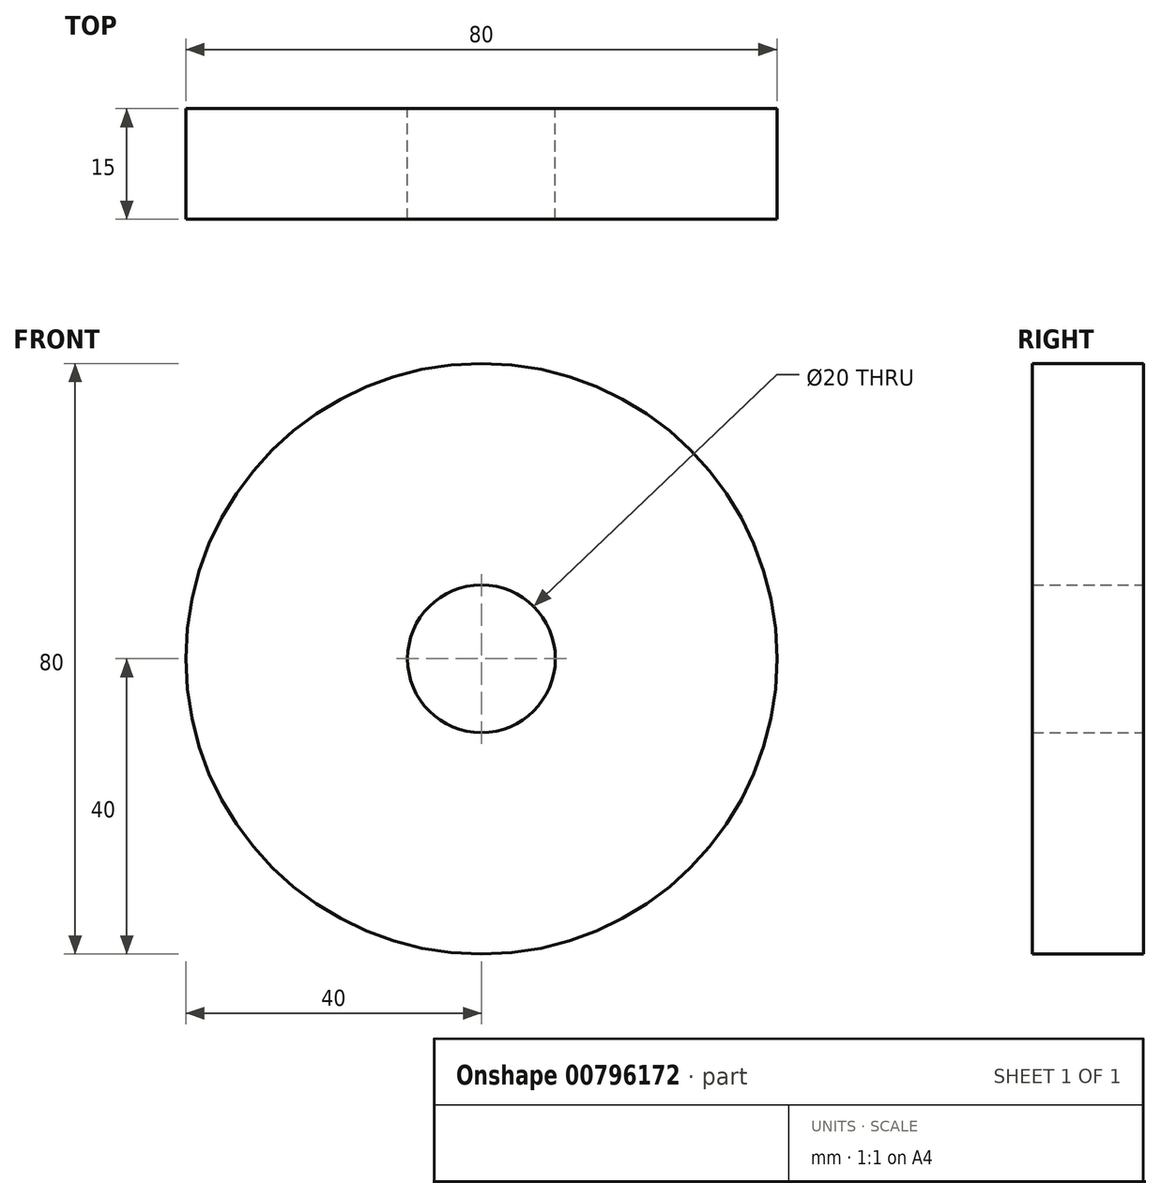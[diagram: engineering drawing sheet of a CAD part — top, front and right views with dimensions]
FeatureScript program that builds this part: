
annotation { "Feature Type Name" : "Feature", "Feature Type Description" : "" }
export const myFeature = defineFeature(function(context is Context, id is Id, definition is map)
    precondition{}
    {
        {
            var Q0;
            Q0=qCreatedBy(makeId("Front.planeOp"),FACE);
            var sketch = newSketch(context, id + "F0", { "sketchPlane" : qUnion([Q0])});
            skCircle(sketch, "E0", {"center": v(0, 0) * mm, "radius": 40 * mm});
            skCircle(sketch, "E1.0", {"center": v(0, 0) * mm, "radius": 10 * mm});
            skSolve(sketch);
        }
        {
            var Q0;
            Q0=makeQuery(id+"F0.imprint","IMPRINT",FACE,{"disambiguationData":[TD([[makeQuery(id+"F0.imprint","IMPRINT",EDGE,{"derivedFrom":sQuery(id+"F0.wireOp",EDGE,"E0")}),1.0]])]});
            extrude(context, id + "F1", {"entities" : qUnion([Q0]), "depth" : 15 * mm, "offsetDistance" : 25 * mm});
        }
    });
